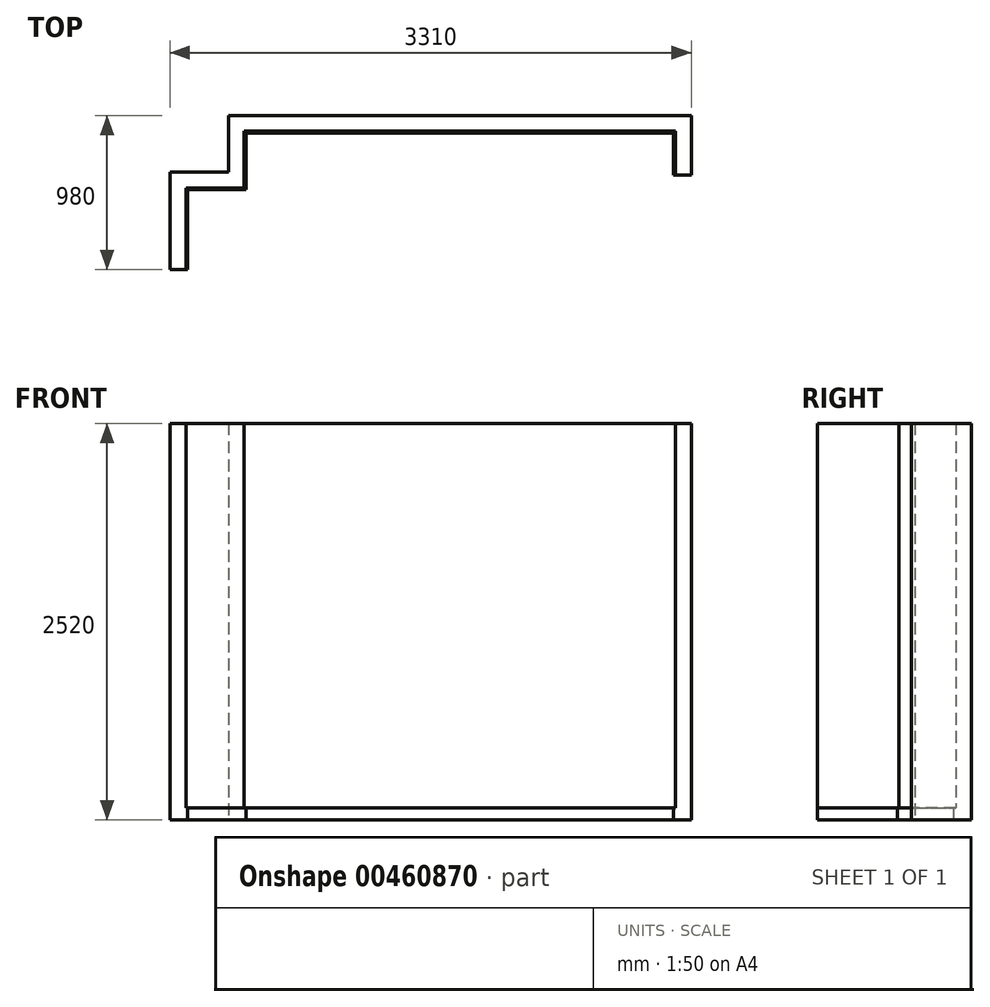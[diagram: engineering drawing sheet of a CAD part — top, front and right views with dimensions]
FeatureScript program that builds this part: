
annotation { "Feature Type Name" : "Feature", "Feature Type Description" : "" }
export const myFeature = defineFeature(function(context is Context, id is Id, definition is map)
    precondition{}
    {
        {
            var Q0;
            Q0=qCreatedBy(makeId("Top.planeOp"),FACE);
            var sketch = newSketch(context, id + "F0", { "sketchPlane" : qUnion([Q0])});
            skLineSegment(sketch, "E0", {"start": v(-370, -564.68) * mm, "end": v(-370, -44.68) * mm});
            skLineSegment(sketch, "E1", {"start": v(-370, -44.68) * mm, "end": v(-370, -44.68) * mm});
            skLineSegment(sketch, "E2", {"start": v(0, -44.68) * mm, "end": v(-370, -44.68) * mm});
            skLineSegment(sketch, "E3", {"start": v(0, -44.68) * mm, "end": v(0, 315.32) * mm});
            skLineSegment(sketch, "E4", {"start": v(0, 315.32) * mm, "end": v(0, 315.32) * mm});
            skLineSegment(sketch, "E5", {"start": v(2740, 315.32) * mm, "end": v(0, 315.32) * mm});
            skLineSegment(sketch, "E6", {"start": v(-370, -564.68) * mm, "end": v(-470, -564.68) * mm});
            skLineSegment(sketch, "E7", {"start": v(-470, -564.68) * mm, "end": v(-470, 55.32) * mm});
            skLineSegment(sketch, "E8", {"start": v(-470, 55.32) * mm, "end": v(-100, 55.32) * mm});
            skLineSegment(sketch, "E9", {"start": v(-100, 55.32) * mm, "end": v(-100, 415.32) * mm});
            skLineSegment(sketch, "E10", {"start": v(-100, 415.32) * mm, "end": v(2840, 415.32) * mm});
            skLineSegment(sketch, "E11", {"start": v(2740, 315.32) * mm, "end": v(2740, 35.32) * mm});
            skLineSegment(sketch, "E12", {"start": v(2740, 35.32) * mm, "end": v(2840, 35.32) * mm});
            skLineSegment(sketch, "E13", {"start": v(2840, 35.32) * mm, "end": v(2840, 415.32) * mm});
            skSolve(sketch);
        }
        {
            var Q0;
            Q0=makeQuery(id+"F0.imprint","IMPRINT",FACE,{"disambiguationData":[TD([[makeQuery(id+"F0.imprint","IMPRINT",EDGE,{"derivedFrom":sQuery(id+"F0.wireOp",EDGE,"E0")}),1.0]])]});
            extrude(context, id + "F1", {"entities" : qUnion([Q0]), "depth" : 2520 * mm});
        }
        {
            var Q0;
            Q0=makeQuery(id+"F1.opExtrude","SWEPT_FACE",FACE,{"disambiguationData":[OSD([sQuery(id+"F0.wireOp",EDGE,"E6")])]});
            var sketch = newSketch(context, id + "F2", { "sketchPlane" : qUnion([Q0])});
            skLineSegment(sketch, "E14.bottom", {"start": v(-370, 0) * mm, "end": v(-358, 0) * mm});
            skLineSegment(sketch, "E14.top", {"start": v(-370, 76) * mm, "end": v(-358, 76) * mm});
            skLineSegment(sketch, "E14.left", {"start": v(-370, 0) * mm, "end": v(-370, 76) * mm});
            skLineSegment(sketch, "E14.right", {"start": v(-358, 0) * mm, "end": v(-358, 76) * mm});
            skSolve(sketch);
        }
        {
            var Q0;
            Q0=makeQuery(id+"F2.imprint","IMPRINT",FACE,{"disambiguationData":[TD([[makeQuery(id+"F2.imprint","IMPRINT",EDGE,{"derivedFrom":sQuery(id+"F2.wireOp",EDGE,"E14.bottom")}),1.0]])]});
            var Q1;
            Q1=makeQuery(id+"F1.opExtrude","CAP_EDGE",EDGE,{"disambiguationData":[OSD([sQuery(id+"F0.wireOp",EDGE,"E0")])],"isStart":true});
            var Q2;
            Q2=makeQuery(id+"F1.opExtrude","CAP_EDGE",EDGE,{"disambiguationData":[OSD([sQuery(id+"F0.wireOp",EDGE,"E2")])],"isStart":true});
            var Q3;
            Q3=makeQuery(id+"F1.opExtrude","CAP_EDGE",EDGE,{"disambiguationData":[OSD([sQuery(id+"F0.wireOp",EDGE,"E3")])],"isStart":true});
            var Q4;
            Q4=makeQuery(id+"F1.opExtrude","CAP_EDGE",EDGE,{"disambiguationData":[OSD([sQuery(id+"F0.wireOp",EDGE,"E5")])],"isStart":true});
            var Q5;
            Q5=makeQuery(id+"F1.opExtrude","CAP_EDGE",EDGE,{"disambiguationData":[OSD([sQuery(id+"F0.wireOp",EDGE,"E11")])],"isStart":true});
            sweep(context, id + "F3", {"operationType" : NewBodyOperationType.ADD, "profiles" : qUnion([Q0]), "path" : qUnion([Q1, Q2, Q3, Q4, Q5])});
        }
    });
